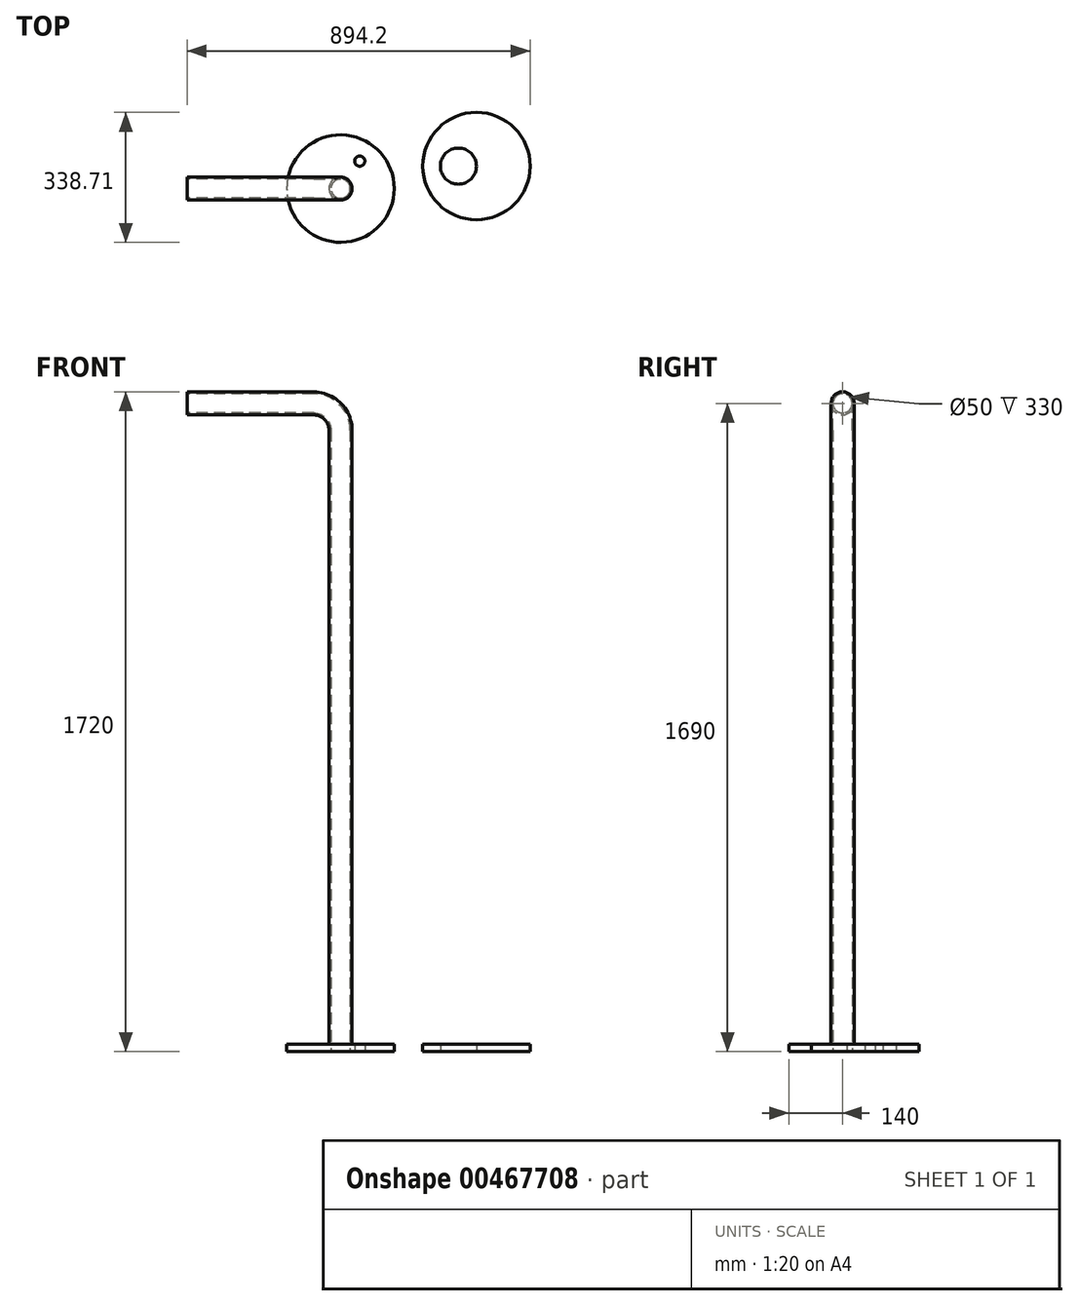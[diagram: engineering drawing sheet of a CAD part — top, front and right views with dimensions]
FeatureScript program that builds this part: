
annotation { "Feature Type Name" : "Feature", "Feature Type Description" : "" }
export const myFeature = defineFeature(function(context is Context, id is Id, definition is map)
    precondition{}
    {
        {
            var Q0;
            Q0=qCreatedBy(makeId("Top.planeOp"),FACE);
            var sketch = newSketch(context, id + "F0", { "sketchPlane" : qUnion([Q0])});
            skCircle(sketch, "E0", {"center": v(0, 0) * mm, "radius": 140 * mm});
            skCircle(sketch, "E1", {"center": v(0, 0) * mm, "radius": 30 * mm});
            skCircle(sketch, "E2", {"center": v(0, 0) * mm, "radius": 25 * mm});
            skCircle(sketch, "E3", {"center": v(49.99, 71.72) * mm, "radius": 13.34 * mm});
            skCircle(sketch, "E4", {"center": v(354.2, 58.7) * mm, "radius": 140 * mm});
            skCircle(sketch, "E5", {"center": v(307.24, 58.7) * mm, "radius": 47 * mm});
            skSolve(sketch);
        }
        {
            var Q0;
            Q0=makeQuery(id+"F0.imprint","IMPRINT",FACE,{"disambiguationData":[TD([[makeQuery(id+"F0.imprint","IMPRINT",EDGE,{"derivedFrom":sQuery(id+"F0.wireOp",EDGE,"E0")}),1.0]])]});
            extrude(context, id + "F1", {"entities" : qUnion([Q0]), "depth" : 20 * mm, "offsetDistance" : 25 * mm});
        }
        {
            var Q0;
            Q0=makeQuery(id+"F0.imprint","IMPRINT",FACE,{"disambiguationData":[TD([[makeQuery(id+"F0.imprint","IMPRINT",EDGE,{"derivedFrom":sQuery(id+"F0.wireOp",EDGE,"E1")}),1.0]])]});
            extrude(context, id + "F2", {"entities" : qUnion([Q0]), "operationType" : NewBodyOperationType.ADD, "depth" : 1620 * mm, "offsetDistance" : 25 * mm});
        }
        {
            var Q0;
            Q0=makeQuery(id+"F2.opExtrude","CAP_FACE",FACE,{"disambiguationData":[OSD([sQuery(id+"F0.wireOp",EDGE,"E1"),sQuery(id+"F0.wireOp",EDGE,"E2")])],"isStart":false});
            cPlane(context, id + "F3", {"entities" : qUnion([Q0]), "cplaneType" : CPlaneType.OFFSET, "offset" : 0 * mm, "width" : 150 * mm, "height" : 150 * mm});
        }
        {
            var Q0;
            Q0=qCreatedBy(id+"F3.planeOp",FACE);
            var sketch = newSketch(context, id + "F4", { "sketchPlane" : qUnion([Q0])});
            skCircle(sketch, "E6.0", {"center": v(0, 0) * mm, "radius": 25 * mm, "construction": true});
            skLineSegment(sketch, "E7", {"start": v(0, 25) * mm, "end": v(0, -25) * mm, "construction": true});
            skLineSegment(sketch, "E8", {"start": v(25, 0) * mm, "end": v(-25, 0) * mm, "construction": true});
            skSolve(sketch);
        }
        {
            var Q0;
            Q0=sQuery(id+"F4.wireOp",EDGE,"E8");
            cPlane(context, id + "F5", {"entities" : qUnion([Q0]), "cplaneType" : CPlaneType.LINE_ANGLE, "offset" : 25 * mm, "angle" : 0 * degree, "width" : 150 * mm, "height" : 150 * mm});
        }
        {
            var Q0;
            Q0=qCreatedBy(id+"F5.planeOp",FACE);
            var sketch = newSketch(context, id + "F6", { "sketchPlane" : qUnion([Q0])});
            skPoint(sketch, "E9.0", {"position": v(0, 1620) * mm});
            skLineSegment(sketch, "E10", {"start": v(0, 1620) * mm, "end": v(0, 1620) * mm});
            skLineSegment(sketch, "E11", {"start": v(-70, 1690) * mm, "end": v(-400, 1690) * mm});
            skPoint(sketch, "E12.visualSharp", {"position": v(0, 1690) * mm});
            skArc(sketch, "E12.filletArc", {"start": v(0, 1620) * mm, "mid": v(-20.5, 1669.5) * mm, "end": v(-70, 1690) * mm});
            skSolve(sketch);
        }
        {
            var Q0;
            Q0=makeQuery(id+"F2.opExtrude","CAP_FACE",FACE,{"disambiguationData":[OSD([sQuery(id+"F0.wireOp",EDGE,"E1"),sQuery(id+"F0.wireOp",EDGE,"E2")])],"isStart":false});
            var Q1;
            Q1=sQuery(id+"F6.wireOp",EDGE,"E12.filletArc");
            var Q2;
            Q2=sQuery(id+"F6.wireOp",EDGE,"E11");
            sweep(context, id + "F7", {"operationType" : NewBodyOperationType.ADD, "profiles" : qUnion([Q0]), "path" : qUnion([Q1, Q2])});
        }
        {
            var Q0;
            Q0=makeQuery(id+"F0.imprint","IMPRINT",FACE,{"disambiguationData":[TD([[makeQuery(id+"F0.imprint","IMPRINT",EDGE,{"derivedFrom":sQuery(id+"F0.wireOp",EDGE,"E4")}),1.0]])]});
            extrude(context, id + "F8", {"entities" : qUnion([Q0]), "depth" : 20 * mm, "offsetDistance" : 25 * mm});
        }
    });
